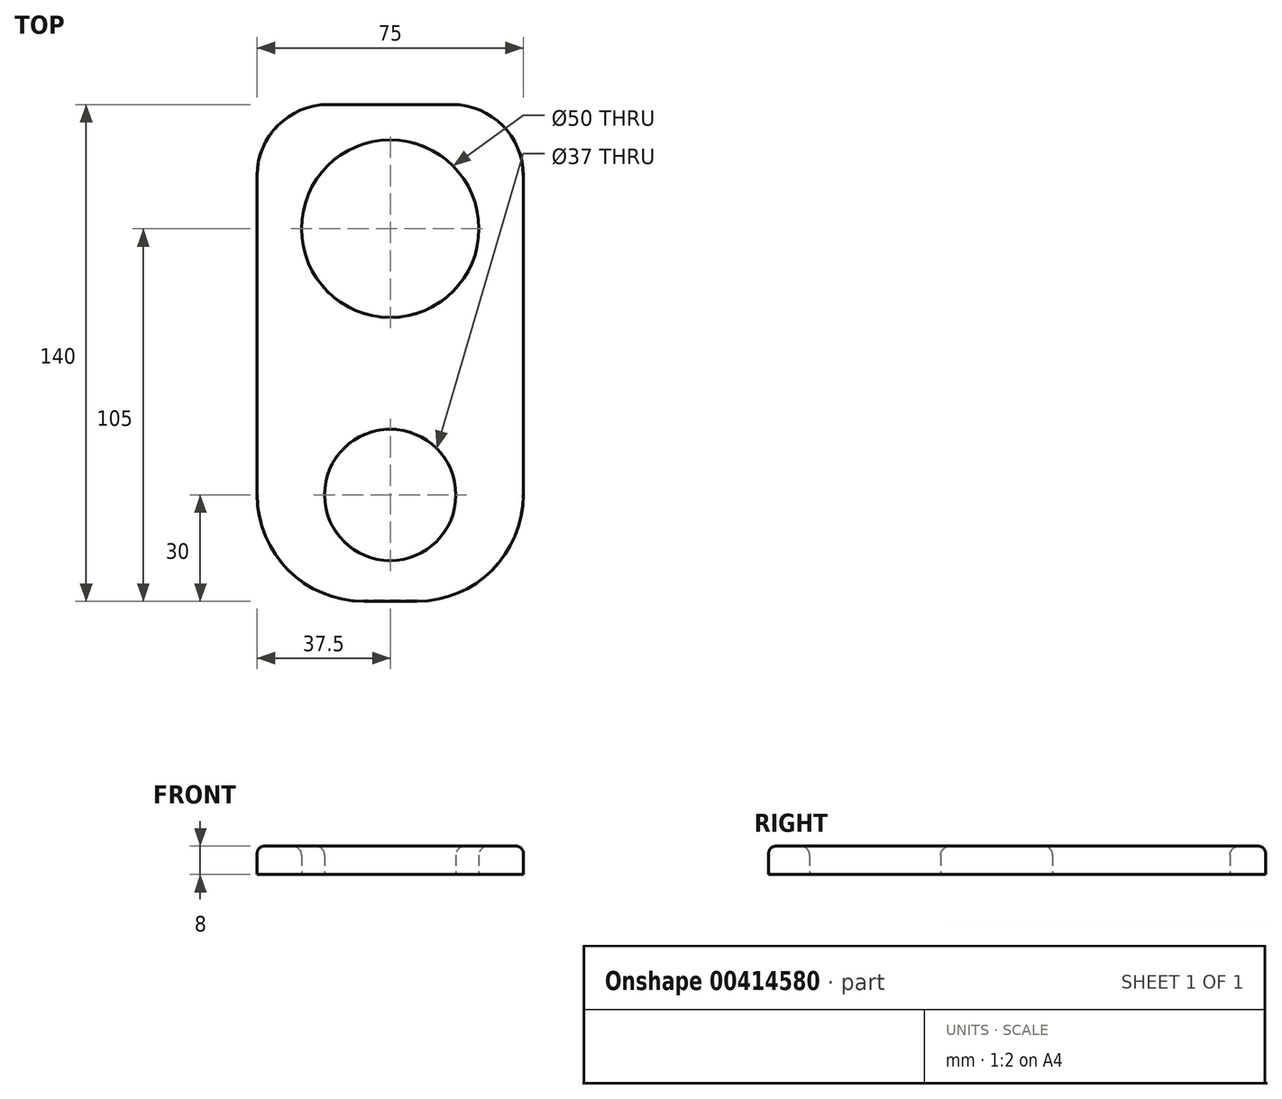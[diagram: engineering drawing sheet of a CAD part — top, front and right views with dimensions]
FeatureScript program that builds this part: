
annotation { "Feature Type Name" : "Feature", "Feature Type Description" : "" }
export const myFeature = defineFeature(function(context is Context, id is Id, definition is map)
    precondition{}
    {
        {
            var Q0;
            Q0=qCreatedBy(makeId("Top.planeOp"),FACE);
            var sketch = newSketch(context, id + "F0", { "sketchPlane" : qUnion([Q0])});
            skLineSegment(sketch, "E0.bottom", {"start": v(0, 0) * mm, "end": v(0, 0) * mm});
            skLineSegment(sketch, "E0.top", {"start": v(0, 0) * mm, "end": v(0, 0) * mm});
            skLineSegment(sketch, "E0.left", {"start": v(0, 0) * mm, "end": v(0, 0) * mm});
            skLineSegment(sketch, "E0.right", {"start": v(0, 0) * mm, "end": v(0, 0) * mm});
            skLineSegment(sketch, "E1.bottom", {"start": v(0, 0) * mm, "end": v(75, 0) * mm});
            skLineSegment(sketch, "E1.top", {"start": v(0, 140) * mm, "end": v(75, 140) * mm});
            skLineSegment(sketch, "E1.left", {"start": v(0, 0) * mm, "end": v(0, 140) * mm});
            skLineSegment(sketch, "E1.right", {"start": v(75, 0) * mm, "end": v(75, 140) * mm});
            skCircle(sketch, "E2", {"center": v(37.5, 105) * mm, "radius": 25 * mm});
            skPoint(sketch, "E2.centerSnap0", {"position": v(37.5, 140) * mm});
            skCircle(sketch, "E3", {"center": v(37.5, 30) * mm, "radius": 18.5 * mm});
            skPoint(sketch, "E3.centerSnap0", {"position": v(37.5, 0) * mm});
            skLineSegment(sketch, "E4", {"start": v(37.5, 105) * mm, "end": v(0, 105) * mm});
            skLineSegment(sketch, "E5", {"start": v(0, 105) * mm, "end": v(37.5, 105) * mm});
            skLineSegment(sketch, "E6", {"start": v(37.5, 105) * mm, "end": v(75, 105) * mm});
            skSolve(sketch);
        }
        {
            var Q0;
            Q0=makeQuery(id+"F0.imprint","IMPRINT",FACE,{"disambiguationData":[TD([[makeQuery(id+"F0.imprint","IMPRINT",EDGE,{"derivedFrom":sQuery(id+"F0.wireOp",EDGE,"E1.bottom")}),1.0]])]});
            var Q1;
            {var subQ1=sQuery(id+"F0.wireOp",EDGE,"E1.top");Q1=makeQuery(id+"F0.imprint","IMPRINT",FACE,{"disambiguationData":[TD([[makeQuery(id+"F0.imprint","IMPRINT",EDGE,{"derivedFrom":subQ1}),-1.0]])]});}
            extrude(context, id + "F1", {"entities" : qUnion([Q0, Q1]), "depth" : 8 * mm});
        }
        {
            var Q0;
            Q0=makeQuery(id+"F1.opExtrude","SWEPT_EDGE",EDGE,{"disambiguationData":[OSD([sQuery(id+"F0.wireOp",EDGE,"E1.bottom"),sQuery(id+"F0.wireOp",EDGE,"E1.right")])]});
            var Q1;
            Q1=makeQuery(id+"F1.opExtrude","SWEPT_EDGE",EDGE,{"disambiguationData":[OSD([sQuery(id+"F0.wireOp",EDGE,"E1.bottom"),sQuery(id+"F0.wireOp",EDGE,"E1.left")])]});
            fillet(context, id + "F2", {"entities" : qUnion([Q0, Q1]), "radius" : 30 * mm, "tangentPropagation" : true, "allowEdgeOverflow" : false});
        }
        {
            var Q0;
            Q0=makeQuery(id+"F1.opExtrude","CAP_EDGE",EDGE,{"disambiguationData":[OSD([sQuery(id+"F0.wireOp",EDGE,"E2")])],"isStart":false});
            var Q1;
            Q1=makeQuery(id+"F1.opExtrude","CAP_EDGE",EDGE,{"disambiguationData":[OSD([sQuery(id+"F0.wireOp",EDGE,"E3")])],"isStart":false});
            fillet(context, id + "F3", {"entities" : qUnion([Q0, Q1]), "radius" : 2.5 * mm, "tangentPropagation" : true, "allowEdgeOverflow" : false});
        }
        {
            var Q0;
            Q0=makeQuery(id+"F1.opExtrude","SWEPT_EDGE",EDGE,{"disambiguationData":[OSD([sQuery(id+"F0.wireOp",EDGE,"E1.top"),sQuery(id+"F0.wireOp",EDGE,"E1.left")])]});
            var Q1;
            Q1=makeQuery(id+"F1.opExtrude","SWEPT_EDGE",EDGE,{"disambiguationData":[OSD([sQuery(id+"F0.wireOp",EDGE,"E1.top"),sQuery(id+"F0.wireOp",EDGE,"E1.right")])]});
            fillet(context, id + "F4", {"entities" : qUnion([Q0, Q1]), "radius" : 20 * mm, "tangentPropagation" : true, "allowEdgeOverflow" : false});
        }
        {
            var Q0;
            {var subQ0=sQuery(id+"F0.wireOp",EDGE,"E1.right");var subQ1=sQuery(id+"F0.wireOp",EDGE,"E1.top");Q0=makeQuery(id+"F4.opFillet","BLEND_EDGE",EDGE,{"blendedFrom":[makeQuery(id+"F1.opExtrude","SWEPT_EDGE",EDGE,{"disambiguationData":[OSD([subQ1,subQ0])]}),makeQuery(id+"F1.opExtrude","CAP_FACE",FACE,{"disambiguationData":[OSD([sQuery(id+"F0.wireOp",EDGE,"E1.bottom"),subQ1,sQuery(id+"F0.wireOp",EDGE,"E1.left"),subQ0,sQuery(id+"F0.wireOp",EDGE,"E2"),sQuery(id+"F0.wireOp",EDGE,"E3")])],"isStart":false})],"blendedInto":[makeQuery(id+"F1.opExtrude","CAP_FACE",FACE,{"disambiguationData":[OSD([sQuery(id+"F0.wireOp",EDGE,"E1.bottom"),subQ1,sQuery(id+"F0.wireOp",EDGE,"E1.left"),subQ0,sQuery(id+"F0.wireOp",EDGE,"E2"),sQuery(id+"F0.wireOp",EDGE,"E3")])],"isStart":false})]});}
            var Q1;
            Q1=makeQuery(id+"F1.opExtrude","CAP_EDGE",EDGE,{"disambiguationData":[OSD([sQuery(id+"F0.wireOp",EDGE,"E1.top")])],"isStart":false});
            var Q2;
            {var subQ0=sQuery(id+"F0.wireOp",EDGE,"E1.left");var subQ1=sQuery(id+"F0.wireOp",EDGE,"E1.top");Q2=makeQuery(id+"F4.opFillet","BLEND_EDGE",EDGE,{"blendedFrom":[makeQuery(id+"F1.opExtrude","SWEPT_EDGE",EDGE,{"disambiguationData":[OSD([subQ1,subQ0])]}),makeQuery(id+"F1.opExtrude","CAP_FACE",FACE,{"disambiguationData":[OSD([sQuery(id+"F0.wireOp",EDGE,"E1.bottom"),subQ1,subQ0,sQuery(id+"F0.wireOp",EDGE,"E1.right"),sQuery(id+"F0.wireOp",EDGE,"E2"),sQuery(id+"F0.wireOp",EDGE,"E3")])],"isStart":false})],"blendedInto":[makeQuery(id+"F1.opExtrude","CAP_FACE",FACE,{"disambiguationData":[OSD([sQuery(id+"F0.wireOp",EDGE,"E1.bottom"),subQ1,subQ0,sQuery(id+"F0.wireOp",EDGE,"E1.right"),sQuery(id+"F0.wireOp",EDGE,"E2"),sQuery(id+"F0.wireOp",EDGE,"E3")])],"isStart":false})]});}
            var Q3;
            Q3=makeQuery(id+"F1.opExtrude","CAP_EDGE",EDGE,{"disambiguationData":[OSD([sQuery(id+"F0.wireOp",EDGE,"E1.left")])],"isStart":false});
            var Q4;
            Q4=makeQuery(id+"F1.opExtrude","CAP_EDGE",EDGE,{"disambiguationData":[OSD([sQuery(id+"F0.wireOp",EDGE,"E1.right")])],"isStart":false});
            var Q5;
            {var subQ0=sQuery(id+"F0.wireOp",EDGE,"E1.right");var subQ1=sQuery(id+"F0.wireOp",EDGE,"E1.bottom");Q5=makeQuery(id+"F2.opFillet","BLEND_EDGE",EDGE,{"blendedFrom":[makeQuery(id+"F1.opExtrude","SWEPT_EDGE",EDGE,{"disambiguationData":[OSD([subQ1,subQ0])]}),makeQuery(id+"F1.opExtrude","CAP_FACE",FACE,{"disambiguationData":[OSD([subQ1,sQuery(id+"F0.wireOp",EDGE,"E1.top"),sQuery(id+"F0.wireOp",EDGE,"E1.left"),subQ0,sQuery(id+"F0.wireOp",EDGE,"E2"),sQuery(id+"F0.wireOp",EDGE,"E3")])],"isStart":false})],"blendedInto":[makeQuery(id+"F1.opExtrude","CAP_FACE",FACE,{"disambiguationData":[OSD([subQ1,sQuery(id+"F0.wireOp",EDGE,"E1.top"),sQuery(id+"F0.wireOp",EDGE,"E1.left"),subQ0,sQuery(id+"F0.wireOp",EDGE,"E2"),sQuery(id+"F0.wireOp",EDGE,"E3")])],"isStart":false})]});}
            var Q6;
            Q6=makeQuery(id+"F1.opExtrude","CAP_EDGE",EDGE,{"disambiguationData":[OSD([sQuery(id+"F0.wireOp",EDGE,"E1.bottom")])],"isStart":false});
            var Q7;
            {var subQ0=sQuery(id+"F0.wireOp",EDGE,"E1.left");var subQ1=sQuery(id+"F0.wireOp",EDGE,"E1.bottom");Q7=makeQuery(id+"F2.opFillet","BLEND_EDGE",EDGE,{"blendedFrom":[makeQuery(id+"F1.opExtrude","SWEPT_EDGE",EDGE,{"disambiguationData":[OSD([subQ1,subQ0])]}),makeQuery(id+"F1.opExtrude","CAP_FACE",FACE,{"disambiguationData":[OSD([subQ1,sQuery(id+"F0.wireOp",EDGE,"E1.top"),subQ0,sQuery(id+"F0.wireOp",EDGE,"E1.right"),sQuery(id+"F0.wireOp",EDGE,"E2"),sQuery(id+"F0.wireOp",EDGE,"E3")])],"isStart":false})],"blendedInto":[makeQuery(id+"F1.opExtrude","CAP_FACE",FACE,{"disambiguationData":[OSD([subQ1,sQuery(id+"F0.wireOp",EDGE,"E1.top"),subQ0,sQuery(id+"F0.wireOp",EDGE,"E1.right"),sQuery(id+"F0.wireOp",EDGE,"E2"),sQuery(id+"F0.wireOp",EDGE,"E3")])],"isStart":false})]});}
            fillet(context, id + "F5", {"entities" : qUnion([Q0, Q1, Q2, Q3, Q4, Q5, Q6, Q7]), "radius" : 2 * mm, "tangentPropagation" : true, "allowEdgeOverflow" : false});
        }
        {
            var Q0;
            Q0=makeQuery(id+"F1.opExtrude","CAP_FACE",FACE,{"disambiguationData":[OSD([sQuery(id+"F0.wireOp",EDGE,"E1.bottom"),sQuery(id+"F0.wireOp",EDGE,"E1.top"),sQuery(id+"F0.wireOp",EDGE,"E1.left"),sQuery(id+"F0.wireOp",EDGE,"E1.right"),sQuery(id+"F0.wireOp",EDGE,"E2"),sQuery(id+"F0.wireOp",EDGE,"E3")])],"isStart":true});
            chamfer(context, id + "F6", {"entities" : qUnion([Q0]), "chamferType" : ChamferType.OFFSET_ANGLE, "width" : .2 * mm, "oppositeDirection" : false, "angle" : 20 * degree});
        }
    });
